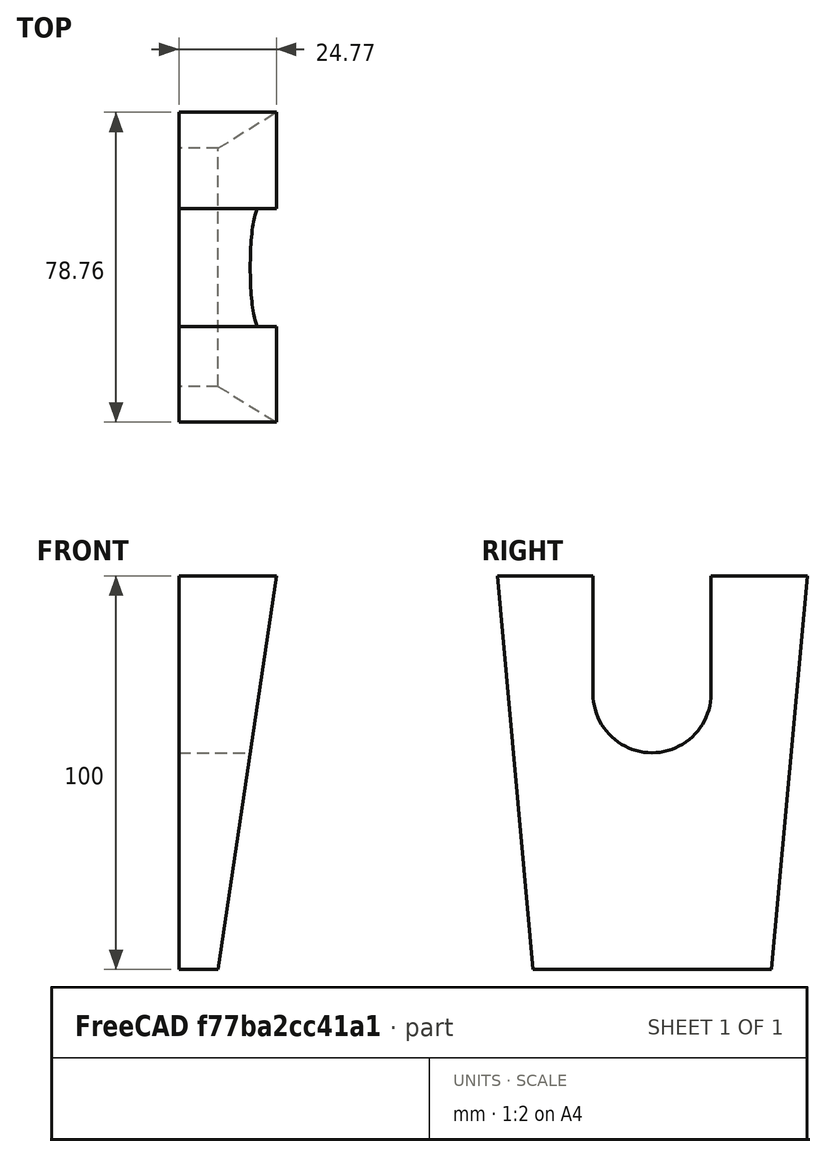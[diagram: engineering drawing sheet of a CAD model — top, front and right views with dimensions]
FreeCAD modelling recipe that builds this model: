
FCSTD DOCUMENT  (FreeCAD 0.14R3702 (Git))
Label: Claptrapface
License: CC-BY 3.0
LicenseURL: http://creativecommons.org/licenses/by/3.0/
objects: Part::Box×5, Part::Cut×4, Part::Cylinder×1, Part::MultiFuse×1
note: 11 computed .brp shape members not serialized (recipe doc carries the construction recipe); baked Part::Feature solids carry a one-line shape summary decoded from their .brp

FEATURE [Part::Box] Box  label="Cube"
  Height = 100
  Length = 25
  Width = 80
FEATURE [Part::Box] Box001  label="Cube001"
  Height = 110
  Length = 19
  Placement = pos=(10,0,0) rot=(0,1,0;0.146608rad)
  Width = 100
FEATURE [Part::Cut] Cut
  Base = -> Box
  Tool = -> Box001
FEATURE [Part::Box] Box003  label="Cube003"
  Height = 120
  Length = 40
  Placement = pos=(0,-30,-4) rot=(1,0,0;0.090757rad)
  Width = 40
FEATURE [Part::Box] Box004  label="Cube002"
  Height = 120
  Length = 40
  Placement = pos=(0,70,-4) rot=(-1,0,0;0.090757rad)
  Width = 40
FEATURE [Part::Cut] Cut001
  Base = -> Cut
  Tool = -> Box003
FEATURE [Part::Cut] Cut002
  Base = -> Cut001
  Tool = -> Box004
FEATURE [Part::Box] Box005  label="Cube004"
  Height = 30
  Length = 100
  Placement = pos=(0,25,70) rot=(0,0,1;0rad)
  Width = 30
FEATURE [Part::Cylinder] Cylinder
  Angle = 360
  Height = 100
  Placement = pos=(0,40,70) rot=(0,1,0;1.5708rad)
  Radius = 15
FEATURE [Part::MultiFuse] Fusion
  Shapes = -> [Box005,Cylinder]
FEATURE [Part::Cut] Cut003
  Base = -> Cut002
  Tool = -> Fusion
